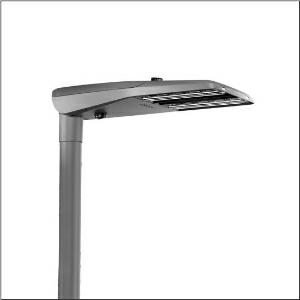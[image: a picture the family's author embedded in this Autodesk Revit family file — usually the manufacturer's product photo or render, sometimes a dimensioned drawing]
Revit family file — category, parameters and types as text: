
# Revit family: streetlight_sl_11_iq_midi___st0_5a_5xc3b51y08le_54cc
name_source: partatom
category: Lighting Fixtures
units: mm (PartAtom-declared; Revit-internal decimal feet)

## family parameters
Cut with Voids When Loaded = No
Host = Face
Light Source = No
Part Type = Normal
Room Calculation Point = No
Round Connector Dimension = Use Diameter
Shared = No

## types (1)
- --- (1 x LED, 9120 lm, 59.4 W, 3000K)
    Apparent Load = 59 VA
    CIE Flux Codes = 43 74 97 100 100
    Color Rendering = 70
    Color Temperature = 3000K
    Default Elevation = 1800 mm
    Description = Streetlight SL 11 iQ midi, mast luminaire, primary light control with 3 zone facetted reflector, of plastic, silver coated, highly specular, primary optical cover: cover, of PMMA, transparent, light distribution: ST0.5a, light emission: direct distribution, primary light characteristic: asymmetric, installation type: post-top, side-entry, LED, High Power LED, rated luminous flux: 9.120lm, luminous efficacy: 155lm/W, light colour: 730, colour temperature: 3000K, control: presetting dimming logarithmic, Street-Remote, Auto-Match, Temp-Guard, Lumen-Switch, Night-Set, Smart-Wire, Light-Fading, Desk-Remote (wireless, voltage-free reading and setting of iQ features in the workshop via application-optimized NFC function/RFID function), optimised constant luminous flux control (CLO 2.0), with cable H07RN-F 5x 1.5mm², mains connection: 220..240V, AC, 50/60Hz, connection cable pre-assembled, cable length: 8,5m, start of lifetime: 59W, end of service life: 62W, reduction: 28W, luminaire housing, of diecast aluminium, powder-coated, Siteco® metallic grey (DB 702S), please order mast flange separately, inclination adjustable without tools: 0°, 5°, 10°, 15° (post-top) | 0°, -5°, -10°, -15° (side-entry), sealing non-destructively replaceable, multi-level sealing system, length: 780mm, width: 376mm, height: 118mm, spigot size: 60/76mm (post-top) and 42/60/76mm (side-entry), mast flange for spigot size: 42mm: 5XC10008XM4, 60mm: 5XC10008XM2, 76/60mm: 5XC10108XM1, equipment: standard, Smart Interface below and above, protection rating (complete): IP66, insulation class (complete): insulation class II (safety insulation), certification: CE, ENEC in preparation, impact resistance: IK09, permissible operating ambient temperature for outdoor applications: -25..+50°C, standard-compliant lighting for roads and squares, packaging unit: 1 piece

Light Distribution: ST0.5a
    Height = 118 mm
    Lamp = 1 x LED
    Lamp Light Flux = 9120 lm
    Lamp Power = 59.4 W
    Lamp count = 1
    Length = 780 mm
    Luminous efficacy = 154 lm/W
    Manufacturer = Siteco
    ModVariant = No
    Model = 5XC3B51Y08LE
    Number of Poles = 1
    OnlyDefault = Yes
    Power Factor = 1
    Product Name = Streetlight SL 11 iQ midi | ST0.5a
    Product group = mast luminaire | pylon top
    ProductGroupID = 6100
    Protection Class = Protection class II
    Protection Degree = IP 66
    RLX_Detail_Level = 1
    RlxData = <blob elided: 74245 chars, md5=0618a50c>
    Socket = socket
    Standby Power = 0 W
    System Light Flux = 9120 lm
    System Power = 59 W
    Type Comments = factory setting: luminous flux: 100 % | dim-lin: 254 | 521 mA
    Type Image = l_1004429.jpg
    URL = http://relux.com
    VarID = @adj_043315
    Voltage = 0 V
    Weight = 0.00 kg
    Width = 376 mm

## geometry (parser evidence)
native form markers: Blend x4, Sweep x11
no freeform markers — native parametric forms only
